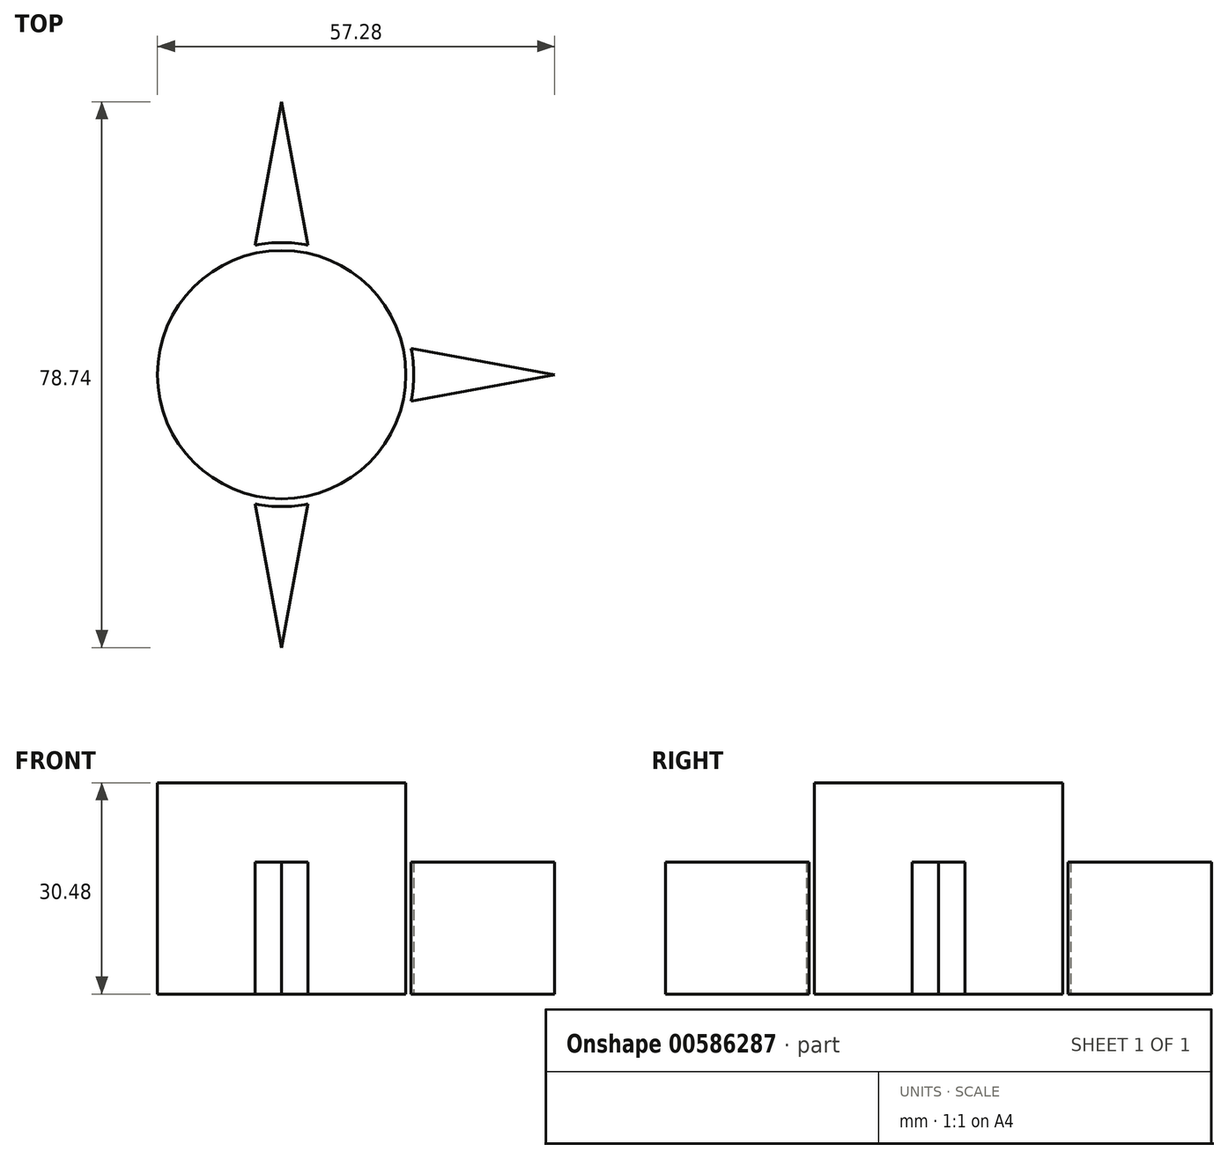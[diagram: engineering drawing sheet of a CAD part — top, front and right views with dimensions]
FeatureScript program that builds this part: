
annotation { "Feature Type Name" : "Feature", "Feature Type Description" : "" }
export const myFeature = defineFeature(function(context is Context, id is Id, definition is map)
    precondition{}
    {
        {
            var Q0;
            Q0=qCreatedBy(makeId("Top.planeOp"),FACE);
            var sketch = newSketch(context, id + "F0", { "sketchPlane" : qUnion([Q0])});
            skCircle(sketch, "E0", {"center": v(0, 0) * mm, "radius": 19.05 * mm});
            skPoint(sketch, "E1", {"position": v(-18.67, 3.81) * mm});
            skPoint(sketch, "E2", {"position": v(-18.67, -3.81) * mm});
            skPoint(sketch, "E3", {"position": v(-19.05, 0) * mm});
            skPoint(sketch, "E4", {"position": v(-39.37, 0) * mm});
            skLineSegment(sketch, "E5", {"start": v(-18.67, -3.8) * mm, "end": v(-39.37, 0) * mm});
            skLineSegment(sketch, "E6", {"start": v(-18.67, 3.8) * mm, "end": v(-39.37, 0) * mm});
            skPoint(sketch, "E7", {"position": v(-3.81, -18.67) * mm});
            skPoint(sketch, "E8", {"position": v(3.81, -18.67) * mm});
            skPoint(sketch, "E9", {"position": v(0, -19.05) * mm});
            skPoint(sketch, "E10", {"position": v(0, -39.37) * mm});
            skLineSegment(sketch, "E11", {"start": v(-3.81, -18.67) * mm, "end": v(0, -39.37) * mm});
            skLineSegment(sketch, "E12", {"start": v(3.81, -18.67) * mm, "end": v(0, -39.37) * mm});
            skLineSegment(sketch, "E13.MirrorCS", {"start": v(-18.67, 3.81) * mm, "end": v(-39.37, 0) * mm});
            skLineSegment(sketch, "E14.MirrorCS", {"start": v(-18.67, -3.81) * mm, "end": v(-39.37, 0) * mm});
            skLineSegment(sketch, "E15.MirrorCS", {"start": v(-3.81, 18.67) * mm, "end": v(0, 39.37) * mm});
            skLineSegment(sketch, "E16.MirrorCS", {"start": v(3.81, 18.67) * mm, "end": v(0, 39.37) * mm});
            skPoint(sketch, "E17.MirrorP", {"position": v(-3.81, 18.67) * mm});
            skPoint(sketch, "E18.MirrorP", {"position": v(0, 19.05) * mm});
            skPoint(sketch, "E19.MirrorP", {"position": v(3.81, 18.67) * mm});
            skPoint(sketch, "E20.MirrorP", {"position": v(0, 39.37) * mm});
            skLineSegment(sketch, "E21.MirrorCS", {"start": v(18.67, 3.81) * mm, "end": v(39.37, 0) * mm});
            skLineSegment(sketch, "E22.MirrorCS", {"start": v(18.67, -3.81) * mm, "end": v(39.37, 0) * mm});
            skPoint(sketch, "E23.MirrorP", {"position": v(39.37, 0) * mm});
            skPoint(sketch, "E24.MirrorP", {"position": v(18.67, 3.81) * mm});
            skPoint(sketch, "E25.MirrorP", {"position": v(19.05, 0) * mm});
            skPoint(sketch, "E26", {"position": v(18.67, -3.81) * mm});
            skSolve(sketch);
        }
        {
            var Q0;
            {var subQ0=sQuery(id+"F0.wireOp",EDGE,"E14.MirrorCS");Q0=makeQuery(id+"F0.imprint","IMPRINT",FACE,{"disambiguationData":[TD([[makeQuery(id+"F0.imprint","IMPRINT",EDGE,{"derivedFrom":subQ0}),-1.0]])]});}
            var Q1;
            {var subQ0=sQuery(id+"F0.wireOp",EDGE,"E0");var subQ5=makeQuery(id+"F0.imprint","INTERSECT",VERTEX,{"derivedFrom":[sQuery(id+"F0.wireOp",EDGE,"E13.MirrorCS"),subQ0]});Q1=makeQuery(id+"F0.imprint","IMPRINT",FACE,{"disambiguationData":[TD([[makeQuery(id+"F0.imprint","IMPRINT",EDGE,{"disambiguationData":[TD([[subQ5,-1.0]])],"derivedFrom":subQ0}),-1.0]])]});}
            var Q2;
            {var subQ0=sQuery(id+"F0.wireOp",EDGE,"E11");Q2=makeQuery(id+"F0.imprint","IMPRINT",FACE,{"disambiguationData":[TD([[makeQuery(id+"F0.imprint","IMPRINT",EDGE,{"derivedFrom":subQ0}),1.0]])]});}
            var Q3;
            {var subQ0=sQuery(id+"F0.wireOp",EDGE,"E21.MirrorCS");Q3=makeQuery(id+"F0.imprint","IMPRINT",FACE,{"disambiguationData":[TD([[makeQuery(id+"F0.imprint","IMPRINT",EDGE,{"derivedFrom":subQ0}),-1.0]])]});}
            var Q4;
            {var subQ0=sQuery(id+"F0.wireOp",EDGE,"E15.MirrorCS");Q4=makeQuery(id+"F0.imprint","IMPRINT",FACE,{"disambiguationData":[TD([[makeQuery(id+"F0.imprint","IMPRINT",EDGE,{"derivedFrom":subQ0}),-1.0]])]});}
            extrude(context, id + "F1", {"entities" : qUnion([Q0, Q1, Q2, Q3, Q4]), "depth" : 19.05 * mm, "offsetDistance" : 25.4 * mm});
        }
        {
            var Q0;
            Q0=qCreatedBy(makeId("Top.planeOp"),FACE);
            var sketch = newSketch(context, id + "F2", { "sketchPlane" : qUnion([Q0])});
            skCircle(sketch, "E27", {"center": v(0, 0) * mm, "radius": 17.9 * mm});
            skSolve(sketch);
        }
        {
            var Q0;
            Q0=makeQuery(id+"F2.imprint","IMPRINT",FACE,{"disambiguationData":[TD([[makeQuery(id+"F2.imprint","IMPRINT",EDGE,{"derivedFrom":sQuery(id+"F2.wireOp",EDGE,"E27")}),1.0]])]});
            extrude(context, id + "F3", {"entities" : qUnion([Q0]), "operationType" : NewBodyOperationType.ADD, "depth" : 30.48 * mm, "offsetDistance" : 25.4 * mm});
        }
    });
